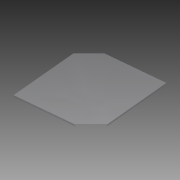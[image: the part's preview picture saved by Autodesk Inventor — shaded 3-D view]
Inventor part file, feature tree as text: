
AUTODESK INVENTOR PART (.ipt)
format: ipt  version: 2015 (Build 190159000, 159)  size: 94,208 bytes
history: native  units: mm
features: reference x4, extrude x1, sketch x1
ambient origin geometry x8: Origin, YZ Plane, XZ Plane, XY Plane, X Axis, Y Axis, Z Axis, Center Point
bodies: Solid1 (feature_tree)
feature tree (6):
  extrude  "Extrusion1"  Depth=5.0mm
  sketch  "Sketch1"  dims[d4=5.0mm d5=0.0mm d6=2.0mm d7=2.0mm d8=2.0mm d9=2.0mm]
  reference  "Reference6"
  reference  "Reference7"
  reference  "Reference8"
  reference  "Reference9"
